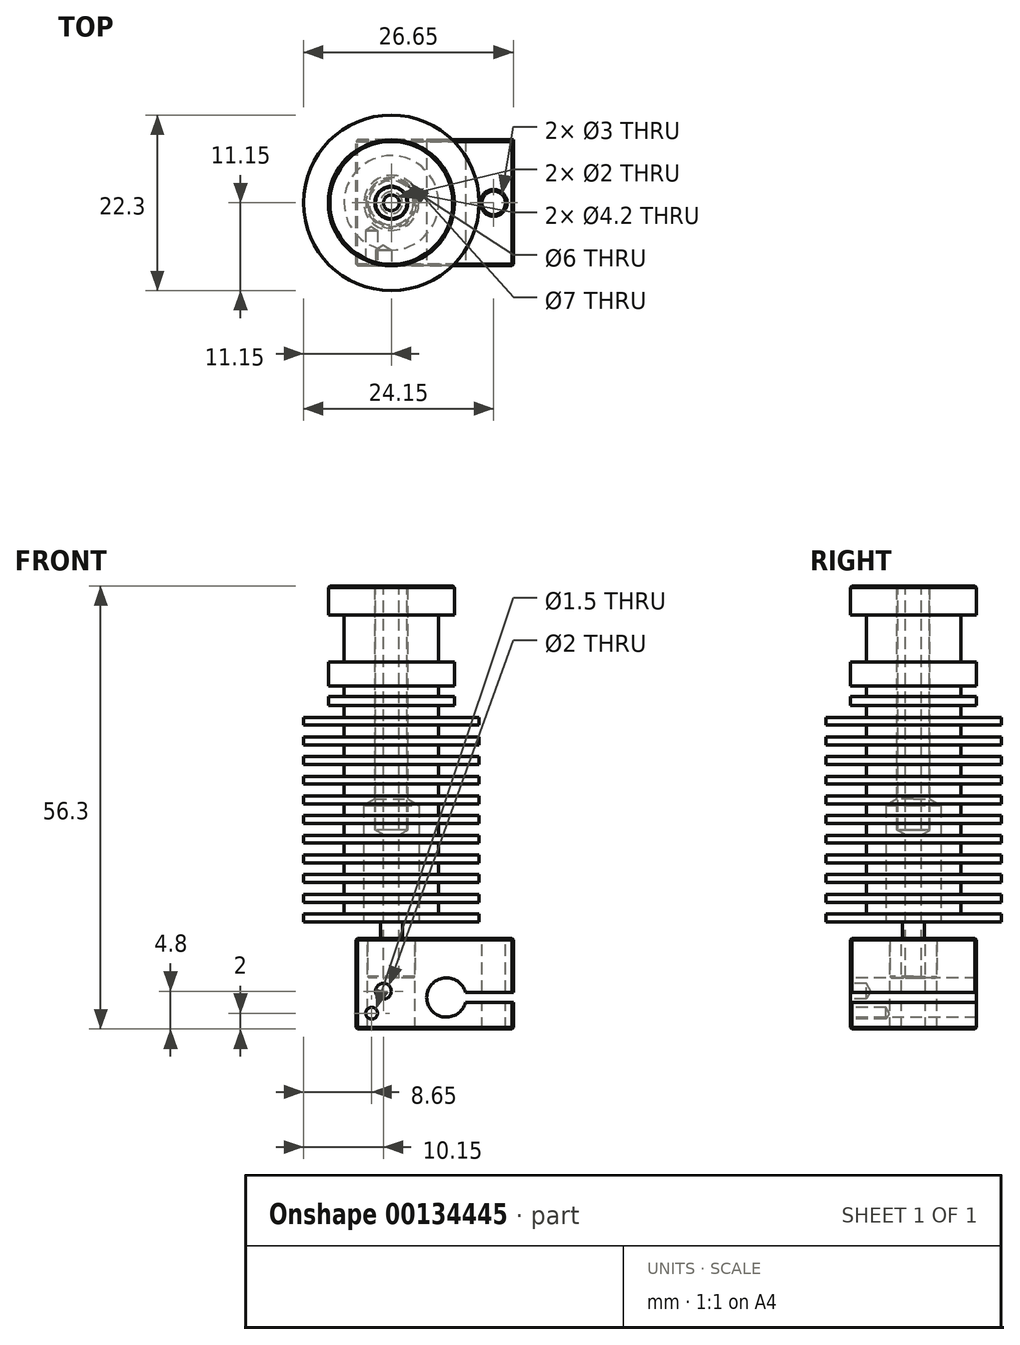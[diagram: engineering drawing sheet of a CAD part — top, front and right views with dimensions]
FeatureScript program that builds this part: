
annotation { "Feature Type Name" : "Feature", "Feature Type Description" : "" }
export const myFeature = defineFeature(function(context is Context, id is Id, definition is map)
    precondition{}
    {
        {
            var Q0;
            Q0=qCreatedBy(makeId("Front.planeOp"),FACE);
            var sketch = newSketch(context, id + "F0", { "sketchPlane" : qUnion([Q0])});
            skLineSegment(sketch, "E0", {"start": v(0, 21.35) * mm, "end": v(8, 21.35) * mm});
            skLineSegment(sketch, "E1", {"start": v(8, 21.35) * mm, "end": v(8, 17.65) * mm});
            skLineSegment(sketch, "E2", {"start": v(8, 17.65) * mm, "end": v(6, 17.65) * mm});
            skLineSegment(sketch, "E3", {"start": v(6, 17.65) * mm, "end": v(6, 11.65) * mm});
            skLineSegment(sketch, "E4", {"start": v(6, 11.65) * mm, "end": v(8, 11.65) * mm});
            skLineSegment(sketch, "E5", {"start": v(8, 11.65) * mm, "end": v(8, 8.65) * mm});
            skLineSegment(sketch, "E6", {"start": v(8, 8.65) * mm, "end": v(6, 8.65) * mm});
            skLineSegment(sketch, "E7", {"start": v(6, 8.65) * mm, "end": v(6, 7.3) * mm});
            skLineSegment(sketch, "E8", {"start": v(6, 7.3) * mm, "end": v(8, 7.3) * mm});
            skLineSegment(sketch, "E9", {"start": v(8, 7.3) * mm, "end": v(8, 6.15) * mm});
            skLineSegment(sketch, "E10", {"start": v(8, 6.15) * mm, "end": v(6, 6.15) * mm});
            skLineSegment(sketch, "E11", {"start": v(6, 6.15) * mm, "end": v(6, 4.65) * mm});
            skLineSegment(sketch, "E12", {"start": v(6, 4.65) * mm, "end": v(11.15, 4.65) * mm});
            skLineSegment(sketch, "E13", {"start": v(11.15, 4.65) * mm, "end": v(11.15, 3.65) * mm});
            skLineSegment(sketch, "E14", {"start": v(11.15, 3.65) * mm, "end": v(6, 3.65) * mm});
            skLineSegment(sketch, "E15.0.1.0", {"start": v(6, 3.65) * mm, "end": v(6, 2.15) * mm});
            skLineSegment(sketch, "E15.0.1.1", {"start": v(6, 2.15) * mm, "end": v(11.15, 2.15) * mm});
            skLineSegment(sketch, "E15.0.1.2", {"start": v(11.15, 2.15) * mm, "end": v(11.15, 1.15) * mm});
            skLineSegment(sketch, "E15.0.1.3", {"start": v(11.15, 1.15) * mm, "end": v(6, 1.15) * mm});
            skLineSegment(sketch, "E15.0.2.0", {"start": v(6, 1.15) * mm, "end": v(6, -0.35) * mm});
            skLineSegment(sketch, "E15.0.2.1", {"start": v(6, -0.35) * mm, "end": v(11.15, -0.35) * mm});
            skLineSegment(sketch, "E15.0.2.2", {"start": v(11.15, -0.35) * mm, "end": v(11.15, -1.35) * mm});
            skLineSegment(sketch, "E15.0.2.3", {"start": v(11.15, -1.35) * mm, "end": v(6, -1.35) * mm});
            skLineSegment(sketch, "E15.0.3.0", {"start": v(6, -1.35) * mm, "end": v(6, -2.85) * mm});
            skLineSegment(sketch, "E15.0.3.1", {"start": v(6, -2.85) * mm, "end": v(11.15, -2.85) * mm});
            skLineSegment(sketch, "E15.0.3.2", {"start": v(11.15, -2.85) * mm, "end": v(11.15, -3.85) * mm});
            skLineSegment(sketch, "E15.0.3.3", {"start": v(11.15, -3.85) * mm, "end": v(6, -3.85) * mm});
            skLineSegment(sketch, "E15.0.4.0", {"start": v(6, -3.85) * mm, "end": v(6, -5.35) * mm});
            skLineSegment(sketch, "E15.0.4.1", {"start": v(6, -5.35) * mm, "end": v(11.15, -5.35) * mm});
            skLineSegment(sketch, "E15.0.4.2", {"start": v(11.15, -5.35) * mm, "end": v(11.15, -6.35) * mm});
            skLineSegment(sketch, "E15.0.4.3", {"start": v(11.15, -6.35) * mm, "end": v(6, -6.35) * mm});
            skLineSegment(sketch, "E15.0.5.0", {"start": v(6, -6.35) * mm, "end": v(6, -7.85) * mm});
            skLineSegment(sketch, "E15.0.5.1", {"start": v(6, -7.85) * mm, "end": v(11.15, -7.85) * mm});
            skLineSegment(sketch, "E15.0.5.2", {"start": v(11.15, -7.85) * mm, "end": v(11.15, -8.85) * mm});
            skLineSegment(sketch, "E15.0.5.3", {"start": v(11.15, -8.85) * mm, "end": v(6, -8.85) * mm});
            skLineSegment(sketch, "E15.0.6.0", {"start": v(6, -8.85) * mm, "end": v(6, -10.35) * mm});
            skLineSegment(sketch, "E15.0.6.1", {"start": v(6, -10.35) * mm, "end": v(11.15, -10.35) * mm});
            skLineSegment(sketch, "E15.0.6.2", {"start": v(11.15, -10.35) * mm, "end": v(11.15, -11.35) * mm});
            skLineSegment(sketch, "E15.0.6.3", {"start": v(11.15, -11.35) * mm, "end": v(6, -11.35) * mm});
            skLineSegment(sketch, "E15.0.7.0", {"start": v(6, -11.35) * mm, "end": v(6, -12.85) * mm});
            skLineSegment(sketch, "E15.0.7.1", {"start": v(6, -12.85) * mm, "end": v(11.15, -12.85) * mm});
            skLineSegment(sketch, "E15.0.7.2", {"start": v(11.15, -12.85) * mm, "end": v(11.15, -13.85) * mm});
            skLineSegment(sketch, "E15.0.7.3", {"start": v(11.15, -13.85) * mm, "end": v(6, -13.85) * mm});
            skLineSegment(sketch, "E15.0.8.0", {"start": v(6, -13.85) * mm, "end": v(6, -15.35) * mm});
            skLineSegment(sketch, "E15.0.8.1", {"start": v(6, -15.35) * mm, "end": v(11.15, -15.35) * mm});
            skLineSegment(sketch, "E15.0.8.2", {"start": v(11.15, -15.35) * mm, "end": v(11.15, -16.35) * mm});
            skLineSegment(sketch, "E15.0.8.3", {"start": v(11.15, -16.35) * mm, "end": v(6, -16.35) * mm});
            skLineSegment(sketch, "E15.0.9.0", {"start": v(6, -16.35) * mm, "end": v(6, -17.85) * mm});
            skLineSegment(sketch, "E15.0.9.1", {"start": v(6, -17.85) * mm, "end": v(11.15, -17.85) * mm});
            skLineSegment(sketch, "E15.0.9.2", {"start": v(11.15, -17.85) * mm, "end": v(11.15, -18.85) * mm});
            skLineSegment(sketch, "E15.0.9.3", {"start": v(11.15, -18.85) * mm, "end": v(6, -18.85) * mm});
            skLineSegment(sketch, "E15.direction1", {"start": v(6, 3.65) * mm, "end": v(31, 3.65) * mm, "construction": true});
            skLineSegment(sketch, "E15.direction2", {"start": v(6, 3.65) * mm, "end": v(6, 1.15) * mm, "construction": true});
            skLineSegment(sketch, "E16", {"start": v(6, -18.85) * mm, "end": v(6, -20.35) * mm});
            skLineSegment(sketch, "E17", {"start": v(6, -20.35) * mm, "end": v(11.15, -20.35) * mm});
            skLineSegment(sketch, "E18", {"start": v(11.15, -20.35) * mm, "end": v(11.15, -21.35) * mm});
            skLineSegment(sketch, "E19", {"start": v(11.15, -21.35) * mm, "end": v(0, -21.35) * mm});
            skLineSegment(sketch, "E20", {"start": v(0, 21.35) * mm, "end": v(0, -21.35) * mm});
            skPoint(sketch, "E21.orphan", {"position": v(6, -21.35) * mm});
            skSolve(sketch);
        }
        {
            var Q0;
            Q0=makeQuery(id+"F0.imprint","IMPRINT",FACE,{"disambiguationData":[TD([[makeQuery(id+"F0.imprint","IMPRINT",EDGE,{"derivedFrom":sQuery(id+"F0.wireOp",EDGE,"E0")}),-1.0]])]});
            var Q1;
            Q1=sQuery(id+"F0.wireOp",EDGE,"E20");
            revolve(context, id + "F1", {"entities" : qUnion([Q0]), "axis" : qUnion([Q1]), "revolveType" : RevolveType.FULL});
        }
        {
            var Q0;
            Q0=makeQuery(id+"F1.opRevolve","SWEPT_FACE",FACE,{"disambiguationData":[OSD([sQuery(id+"F0.wireOp",EDGE,"E19")])]});
            var sketch = newSketch(context, id + "F2", { "sketchPlane" : qUnion([Q0])});
            skPoint(sketch, "E22", {"position": v(0, 0) * mm});
            skSolve(sketch);
        }
        {
            var Q0;
            Q0=sQuery(id+"F2.wireOp",VERTEX,"E22");
            var Q1;
            Q1=makeQuery(id+"F1.opRevolve","SWEPT_BODY",BODY,{"disambiguationData":[OSD([sQuery(id+"F0.wireOp",EDGE,"E0"),sQuery(id+"F0.wireOp",EDGE,"E1"),sQuery(id+"F0.wireOp",EDGE,"E2"),sQuery(id+"F0.wireOp",EDGE,"E3"),sQuery(id+"F0.wireOp",EDGE,"E4"),sQuery(id+"F0.wireOp",EDGE,"E5"),sQuery(id+"F0.wireOp",EDGE,"E6"),sQuery(id+"F0.wireOp",EDGE,"E7"),sQuery(id+"F0.wireOp",EDGE,"E8"),sQuery(id+"F0.wireOp",EDGE,"E9"),sQuery(id+"F0.wireOp",EDGE,"E10"),sQuery(id+"F0.wireOp",EDGE,"E11"),sQuery(id+"F0.wireOp",EDGE,"E12"),sQuery(id+"F0.wireOp",EDGE,"E13"),sQuery(id+"F0.wireOp",EDGE,"E14"),sQuery(id+"F0.wireOp",EDGE,"E15.0.1.0"),sQuery(id+"F0.wireOp",EDGE,"E15.0.1.1"),sQuery(id+"F0.wireOp",EDGE,"E15.0.1.2"),sQuery(id+"F0.wireOp",EDGE,"E15.0.1.3"),sQuery(id+"F0.wireOp",EDGE,"E15.0.2.0"),sQuery(id+"F0.wireOp",EDGE,"E15.0.2.1"),sQuery(id+"F0.wireOp",EDGE,"E15.0.2.2"),sQuery(id+"F0.wireOp",EDGE,"E15.0.2.3"),sQuery(id+"F0.wireOp",EDGE,"E15.0.3.0"),sQuery(id+"F0.wireOp",EDGE,"E15.0.3.1"),sQuery(id+"F0.wireOp",EDGE,"E15.0.3.2"),sQuery(id+"F0.wireOp",EDGE,"E15.0.3.3"),sQuery(id+"F0.wireOp",EDGE,"E15.0.4.0"),sQuery(id+"F0.wireOp",EDGE,"E15.0.4.1"),sQuery(id+"F0.wireOp",EDGE,"E15.0.4.2"),sQuery(id+"F0.wireOp",EDGE,"E15.0.4.3"),sQuery(id+"F0.wireOp",EDGE,"E15.0.5.0"),sQuery(id+"F0.wireOp",EDGE,"E15.0.5.1"),sQuery(id+"F0.wireOp",EDGE,"E15.0.5.2"),sQuery(id+"F0.wireOp",EDGE,"E15.0.5.3"),sQuery(id+"F0.wireOp",EDGE,"E15.0.6.0"),sQuery(id+"F0.wireOp",EDGE,"E15.0.6.1"),sQuery(id+"F0.wireOp",EDGE,"E15.0.6.2"),sQuery(id+"F0.wireOp",EDGE,"E15.0.6.3"),sQuery(id+"F0.wireOp",EDGE,"E15.0.7.0"),sQuery(id+"F0.wireOp",EDGE,"E15.0.7.1"),sQuery(id+"F0.wireOp",EDGE,"E15.0.7.2"),sQuery(id+"F0.wireOp",EDGE,"E15.0.7.3"),sQuery(id+"F0.wireOp",EDGE,"E15.0.8.0"),sQuery(id+"F0.wireOp",EDGE,"E15.0.8.1"),sQuery(id+"F0.wireOp",EDGE,"E15.0.8.2"),sQuery(id+"F0.wireOp",EDGE,"E15.0.8.3"),sQuery(id+"F0.wireOp",EDGE,"E15.0.9.0"),sQuery(id+"F0.wireOp",EDGE,"E15.0.9.1"),sQuery(id+"F0.wireOp",EDGE,"E15.0.9.2"),sQuery(id+"F0.wireOp",EDGE,"E15.0.9.3"),sQuery(id+"F0.wireOp",EDGE,"E16"),sQuery(id+"F0.wireOp",EDGE,"E17"),sQuery(id+"F0.wireOp",EDGE,"E18"),sQuery(id+"F0.wireOp",EDGE,"E19"),sQuery(id+"F0.wireOp",EDGE,"E20")])]});
            hole(context, id + "F3", {"style" : HoleStyle.SIMPLE, "endStyle" : HoleEndStyle.BLIND, "holeDiameter" : 7 * mm, "holeDepth" : 14.8 * mm, "locations" : qUnion([Q0]), "scope" : qUnion([Q1])});
        }
        {
            var Q0;
            Q0=qCreatedBy(makeId("Front.planeOp"),FACE);
            var sketch = newSketch(context, id + "F4", { "sketchPlane" : qUnion([Q0])});
            skLineSegment(sketch, "E23", {"start": v(0, -6.55) * mm, "end": v(3.5, -6.55) * mm});
            skLineSegment(sketch, "E24", {"start": v(3.5, -6.55) * mm, "end": v(3.5, -21.35) * mm});
            skLineSegment(sketch, "E25", {"start": v(3.5, -21.35) * mm, "end": v(1.4, -21.35) * mm});
            skLineSegment(sketch, "E26", {"start": v(1.4, -21.35) * mm, "end": v(1.4, -23.45) * mm});
            skLineSegment(sketch, "E27", {"start": v(1.4, -23.45) * mm, "end": v(3, -23.45) * mm});
            skLineSegment(sketch, "E28", {"start": v(3, -23.45) * mm, "end": v(3, -28.45) * mm});
            skLineSegment(sketch, "E29", {"start": v(3, -28.45) * mm, "end": v(0, -28.45) * mm});
            skLineSegment(sketch, "E30", {"start": v(0, -28.45) * mm, "end": v(0, -6.55) * mm});
            skLineSegment(sketch, "E31.0", {"start": v(3.5, -21.35) * mm, "end": v(-3.5, -21.35) * mm, "construction": true});
            skSolve(sketch);
        }
        {
            var Q0;
            Q0=qSketchRegion(id+"F4",true);
            var Q1;
            Q1=sQuery(id+"F4.wireOp",EDGE,"E30");
            revolve(context, id + "F5", {"entities" : qUnion([Q0]), "axis" : qUnion([Q1]), "revolveType" : RevolveType.FULL});
        }
        {
            var Q0;
            Q0=makeQuery(id+"F5.opRevolve","SWEPT_FACE",FACE,{"disambiguationData":[OSD([sQuery(id+"F4.wireOp",EDGE,"E23")])]});
            var sketch = newSketch(context, id + "F6", { "sketchPlane" : qUnion([Q0])});
            skPoint(sketch, "E32", {"position": v(0, 0) * mm});
            skSolve(sketch);
        }
        {
            var Q0;
            Q0=sQuery(id+"F6.wireOp",VERTEX,"E32");
            var Q1;
            Q1=makeQuery(id+"F5.opRevolve","SWEPT_BODY",BODY,{"disambiguationData":[OSD([sQuery(id+"F4.wireOp",EDGE,"E23"),sQuery(id+"F4.wireOp",EDGE,"E24"),sQuery(id+"F4.wireOp",EDGE,"E25"),sQuery(id+"F4.wireOp",EDGE,"E26"),sQuery(id+"F4.wireOp",EDGE,"E27"),sQuery(id+"F4.wireOp",EDGE,"E28"),sQuery(id+"F4.wireOp",EDGE,"E29"),sQuery(id+"F4.wireOp",EDGE,"E30")])]});
            hole(context, id + "F7", {"style" : HoleStyle.SIMPLE, "endStyle" : HoleEndStyle.THROUGH, "holeDiameter" : 2 * mm, "locations" : qUnion([Q0]), "scope" : qUnion([Q1]), "isTappedThrough" : true});
        }
        {
            var Q0;
            Q0=makeQuery(id+"F1.opRevolve","SWEPT_FACE",FACE,{"disambiguationData":[OSD([sQuery(id+"F0.wireOp",EDGE,"E0")])]});
            var sketch = newSketch(context, id + "F8", { "sketchPlane" : qUnion([Q0])});
            skPoint(sketch, "E33", {"position": v(0, 0) * mm});
            skSolve(sketch);
        }
        {
            var Q0;
            Q0=sQuery(id+"F8.wireOp",VERTEX,"E33");
            var Q1;
            Q1=makeQuery(id+"F1.opRevolve","SWEPT_BODY",BODY,{"disambiguationData":[OSD([sQuery(id+"F0.wireOp",EDGE,"E0"),sQuery(id+"F0.wireOp",EDGE,"E1"),sQuery(id+"F0.wireOp",EDGE,"E2"),sQuery(id+"F0.wireOp",EDGE,"E3"),sQuery(id+"F0.wireOp",EDGE,"E4"),sQuery(id+"F0.wireOp",EDGE,"E5"),sQuery(id+"F0.wireOp",EDGE,"E6"),sQuery(id+"F0.wireOp",EDGE,"E7"),sQuery(id+"F0.wireOp",EDGE,"E8"),sQuery(id+"F0.wireOp",EDGE,"E9"),sQuery(id+"F0.wireOp",EDGE,"E10"),sQuery(id+"F0.wireOp",EDGE,"E11"),sQuery(id+"F0.wireOp",EDGE,"E12"),sQuery(id+"F0.wireOp",EDGE,"E13"),sQuery(id+"F0.wireOp",EDGE,"E14"),sQuery(id+"F0.wireOp",EDGE,"E15.0.1.0"),sQuery(id+"F0.wireOp",EDGE,"E15.0.1.1"),sQuery(id+"F0.wireOp",EDGE,"E15.0.1.2"),sQuery(id+"F0.wireOp",EDGE,"E15.0.1.3"),sQuery(id+"F0.wireOp",EDGE,"E15.0.2.0"),sQuery(id+"F0.wireOp",EDGE,"E15.0.2.1"),sQuery(id+"F0.wireOp",EDGE,"E15.0.2.2"),sQuery(id+"F0.wireOp",EDGE,"E15.0.2.3"),sQuery(id+"F0.wireOp",EDGE,"E15.0.3.0"),sQuery(id+"F0.wireOp",EDGE,"E15.0.3.1"),sQuery(id+"F0.wireOp",EDGE,"E15.0.3.2"),sQuery(id+"F0.wireOp",EDGE,"E15.0.3.3"),sQuery(id+"F0.wireOp",EDGE,"E15.0.4.0"),sQuery(id+"F0.wireOp",EDGE,"E15.0.4.1"),sQuery(id+"F0.wireOp",EDGE,"E15.0.4.2"),sQuery(id+"F0.wireOp",EDGE,"E15.0.4.3"),sQuery(id+"F0.wireOp",EDGE,"E15.0.5.0"),sQuery(id+"F0.wireOp",EDGE,"E15.0.5.1"),sQuery(id+"F0.wireOp",EDGE,"E15.0.5.2"),sQuery(id+"F0.wireOp",EDGE,"E15.0.5.3"),sQuery(id+"F0.wireOp",EDGE,"E15.0.6.0"),sQuery(id+"F0.wireOp",EDGE,"E15.0.6.1"),sQuery(id+"F0.wireOp",EDGE,"E15.0.6.2"),sQuery(id+"F0.wireOp",EDGE,"E15.0.6.3"),sQuery(id+"F0.wireOp",EDGE,"E15.0.7.0"),sQuery(id+"F0.wireOp",EDGE,"E15.0.7.1"),sQuery(id+"F0.wireOp",EDGE,"E15.0.7.2"),sQuery(id+"F0.wireOp",EDGE,"E15.0.7.3"),sQuery(id+"F0.wireOp",EDGE,"E15.0.8.0"),sQuery(id+"F0.wireOp",EDGE,"E15.0.8.1"),sQuery(id+"F0.wireOp",EDGE,"E15.0.8.2"),sQuery(id+"F0.wireOp",EDGE,"E15.0.8.3"),sQuery(id+"F0.wireOp",EDGE,"E15.0.9.0"),sQuery(id+"F0.wireOp",EDGE,"E15.0.9.1"),sQuery(id+"F0.wireOp",EDGE,"E15.0.9.2"),sQuery(id+"F0.wireOp",EDGE,"E15.0.9.3"),sQuery(id+"F0.wireOp",EDGE,"E16"),sQuery(id+"F0.wireOp",EDGE,"E17"),sQuery(id+"F0.wireOp",EDGE,"E18"),sQuery(id+"F0.wireOp",EDGE,"E19"),sQuery(id+"F0.wireOp",EDGE,"E20")])]});
            var Q2;
            Q2=makeQuery(id+"F5.opRevolve","SWEPT_BODY",BODY,{"disambiguationData":[OSD([sQuery(id+"F4.wireOp",EDGE,"E23"),sQuery(id+"F4.wireOp",EDGE,"E24"),sQuery(id+"F4.wireOp",EDGE,"E25"),sQuery(id+"F4.wireOp",EDGE,"E26"),sQuery(id+"F4.wireOp",EDGE,"E27"),sQuery(id+"F4.wireOp",EDGE,"E28"),sQuery(id+"F4.wireOp",EDGE,"E29"),sQuery(id+"F4.wireOp",EDGE,"E30")])]});
            hole(context, id + "F9", {"style" : HoleStyle.SIMPLE, "endStyle" : HoleEndStyle.BLIND, "holeDiameter" : 4.2 * mm, "holeDepth" : 31 * mm, "locations" : qUnion([Q0]), "scope" : qUnion([Q1, Q2])});
        }
        {
            var Q0;
            Q0=qCreatedBy(makeId("Front.planeOp"),FACE);
            var sketch = newSketch(context, id + "F10", { "sketchPlane" : qUnion([Q0])});
            skLineSegment(sketch, "E34.0", {"start": v(-2.1, -9.65) * mm, "end": v(2.1, -9.65) * mm, "construction": true});
            skLineSegment(sketch, "E35.bottom", {"start": v(1, 21.35) * mm, "end": v(2, 21.35) * mm});
            skLineSegment(sketch, "E35.top", {"start": v(1, -9.65) * mm, "end": v(2, -9.65) * mm});
            skLineSegment(sketch, "E35.left", {"start": v(1, 21.35) * mm, "end": v(1, -9.65) * mm});
            skLineSegment(sketch, "E35.right", {"start": v(2, 21.35) * mm, "end": v(2, -9.65) * mm});
            skLineSegment(sketch, "E36", {"start": v(0, 26.07) * mm, "end": v(0, -35.6) * mm, "construction": true});
            skLineSegment(sketch, "E37.0", {"start": v(-2.1, 21.35) * mm, "end": v(2.1, 21.35) * mm, "construction": true});
            skSolve(sketch);
        }
        {
            var Q0;
            Q0=qSketchRegion(id+"F10",true);
            var Q1;
            Q1=qConstructionFilter(qBodyType(qCreatedBy(id+"F10",EDGE),BodyType.WIRE),ConstructionObject.NO);
            var Q2;
            Q2=sQuery(id+"F10.wireOp",EDGE,"E36");
            revolve(context, id + "F11", {"entities" : qUnion([Q0]), "surfaceEntities" : qUnion([Q1]), "axis" : qUnion([Q2]), "revolveType" : RevolveType.FULL});
        }
        {
            var Q0;
            Q0=makeQuery(id+"F5.opRevolve","SWEPT_FACE",FACE,{"disambiguationData":[OSD([sQuery(id+"F4.wireOp",EDGE,"E27")])]});
            var sketch = newSketch(context, id + "F12", { "sketchPlane" : qUnion([Q0])});
            skLineSegment(sketch, "E38.bottom", {"start": v(-4.5, -8) * mm, "end": v(15.5, -8) * mm});
            skLineSegment(sketch, "E38.top", {"start": v(-4.5, 8) * mm, "end": v(15.5, 8) * mm});
            skLineSegment(sketch, "E38.left", {"start": v(-4.5, -8) * mm, "end": v(-4.5, 8) * mm});
            skLineSegment(sketch, "E38.right", {"start": v(15.5, -8) * mm, "end": v(15.5, 8) * mm});
            skPoint(sketch, "E39", {"position": v(0, 0) * mm});
            skPoint(sketch, "E40", {"position": v(13, 0) * mm});
            skSolve(sketch);
        }
        {
            var Q0;
            Q0=qSketchRegion(id+"F12",true);
            extrude(context, id + "F13", {"entities" : qUnion([Q0]), "oppositeDirection" : true, "depth" : 11.5 * mm});
        }
        {
            var Q0;
            Q0=sQuery(id+"F12.wireOp",VERTEX,"E39");
            var Q1;
            Q1=makeQuery(id+"F13.opExtrude","SWEPT_BODY",BODY,{"disambiguationData":[OSD([sQuery(id+"F12.wireOp",EDGE,"E38.bottom"),sQuery(id+"F12.wireOp",EDGE,"E38.top"),sQuery(id+"F12.wireOp",EDGE,"E38.left"),sQuery(id+"F12.wireOp",EDGE,"E38.right")])]});
            hole(context, id + "F14", {"style" : HoleStyle.SIMPLE, "endStyle" : HoleEndStyle.THROUGH, "holeDiameter" : 6 * mm, "locations" : qUnion([Q0]), "scope" : qUnion([Q1]), "isTappedThrough" : true});
        }
        {
            var Q0;
            Q0=sQuery(id+"F12.wireOp",VERTEX,"E40");
            var Q1;
            Q1=makeQuery(id+"F13.opExtrude","SWEPT_BODY",BODY,{"disambiguationData":[OSD([sQuery(id+"F12.wireOp",EDGE,"E38.bottom"),sQuery(id+"F12.wireOp",EDGE,"E38.top"),sQuery(id+"F12.wireOp",EDGE,"E38.left"),sQuery(id+"F12.wireOp",EDGE,"E38.right")])]});
            hole(context, id + "F15", {"style" : HoleStyle.SIMPLE, "endStyle" : HoleEndStyle.THROUGH, "holeDiameter" : 3 * mm, "locations" : qUnion([Q0]), "scope" : qUnion([Q1]), "isTappedThrough" : true});
        }
        {
            var Q0;
            Q0=makeQuery(id+"F13.opExtrude","SWEPT_FACE",FACE,{"disambiguationData":[OSD([sQuery(id+"F12.wireOp",EDGE,"E38.bottom")])]});
            var sketch = newSketch(context, id + "F16", { "sketchPlane" : qUnion([Q0])});
            skPoint(sketch, "E41", {"position": v(-1, -30.15) * mm});
            skPoint(sketch, "E42", {"position": v(-2.5, -32.95) * mm});
            skPoint(sketch, "E43", {"position": v(7, -30.95) * mm});
            skLineSegment(sketch, "E44.bottom", {"start": v(15.5, -30.3) * mm, "end": v(7, -30.3) * mm});
            skLineSegment(sketch, "E44.top", {"start": v(15.5, -31.6) * mm, "end": v(7, -31.6) * mm});
            skLineSegment(sketch, "E44.left", {"start": v(15.5, -30.3) * mm, "end": v(15.5, -31.6) * mm});
            skLineSegment(sketch, "E44.right", {"start": v(7, -30.3) * mm, "end": v(7, -31.6) * mm});
            skSolve(sketch);
        }
        {
            var Q0;
            Q0=sQuery(id+"F16.wireOp",VERTEX,"E42");
            var Q1;
            Q1=makeQuery(id+"F13.opExtrude","SWEPT_BODY",BODY,{"disambiguationData":[OSD([sQuery(id+"F12.wireOp",EDGE,"E38.bottom"),sQuery(id+"F12.wireOp",EDGE,"E38.top"),sQuery(id+"F12.wireOp",EDGE,"E38.left"),sQuery(id+"F12.wireOp",EDGE,"E38.right")])]});
            hole(context, id + "F17", {"style" : HoleStyle.SIMPLE, "endStyle" : HoleEndStyle.BLIND, "holeDiameter" : 1.5 * mm, "holeDepth" : 4.5 * mm, "locations" : qUnion([Q0]), "scope" : qUnion([Q1])});
        }
        {
            var Q0;
            Q0=sQuery(id+"F16.wireOp",VERTEX,"E41");
            var Q1;
            Q1=makeQuery(id+"F13.opExtrude","SWEPT_BODY",BODY,{"disambiguationData":[OSD([sQuery(id+"F12.wireOp",EDGE,"E38.bottom"),sQuery(id+"F12.wireOp",EDGE,"E38.top"),sQuery(id+"F12.wireOp",EDGE,"E38.left"),sQuery(id+"F12.wireOp",EDGE,"E38.right")])]});
            hole(context, id + "F18", {"style" : HoleStyle.SIMPLE, "endStyle" : HoleEndStyle.BLIND, "holeDiameter" : 2 * mm, "holeDepth" : 2 * mm, "locations" : qUnion([Q0]), "scope" : qUnion([Q1])});
        }
        {
            var Q0;
            Q0=sQuery(id+"F16.wireOp",VERTEX,"E43");
            var Q1;
            Q1=makeQuery(id+"F13.opExtrude","SWEPT_BODY",BODY,{"disambiguationData":[OSD([sQuery(id+"F12.wireOp",EDGE,"E38.bottom"),sQuery(id+"F12.wireOp",EDGE,"E38.top"),sQuery(id+"F12.wireOp",EDGE,"E38.left"),sQuery(id+"F12.wireOp",EDGE,"E38.right")])]});
            hole(context, id + "F19", {"style" : HoleStyle.SIMPLE, "endStyle" : HoleEndStyle.THROUGH, "holeDiameter" : 5 * mm, "locations" : qUnion([Q0]), "scope" : qUnion([Q1]), "isTappedThrough" : true});
        }
        {
            var Q0;
            Q0=makeQuery(id+"F16.imprint","IMPRINT",FACE,{"disambiguationData":[TD([[makeQuery(id+"F16.imprint","IMPRINT",EDGE,{"derivedFrom":sQuery(id+"F16.wireOp",EDGE,"E44.bottom")}),1.0]])]});
            var Q1;
            Q1=makeQuery(id+"F13.opExtrude","SWEPT_BODY",BODY,{"disambiguationData":[OSD([sQuery(id+"F12.wireOp",EDGE,"E38.bottom"),sQuery(id+"F12.wireOp",EDGE,"E38.top"),sQuery(id+"F12.wireOp",EDGE,"E38.left"),sQuery(id+"F12.wireOp",EDGE,"E38.right")])]});
            extrude(context, id + "F20", {"entities" : qUnion([Q0]), "operationType" : NewBodyOperationType.REMOVE, "endBound" : BoundingType.UP_TO_BODY, "oppositeDirection" : true, "endBoundEntityBody" : qUnion([Q1]), "depth" : 25 * mm});
        }
        {
            var Q0;
            Q0=makeQuery(id+"F1.opRevolve","SWEPT_EDGE",EDGE,{"disambiguationData":[OSD([sQuery(id+"F0.wireOp",EDGE,"E0"),sQuery(id+"F0.wireOp",EDGE,"E1")])]});
            var Q1;
            Q1=makeQuery(id+"F3.hole-0.boolean.opBoolean","COPY",EDGE,{"derivedFrom":makeQuery(id+"F3.hole-0.opRevolve","SWEPT_EDGE",EDGE,{"disambiguationData":[OSD([sQuery(id+"F3.hole-0.sketch.wireOp",EDGE,"core_line_2"),sQuery(id+"F3.hole-0.sketch.wireOp",EDGE,"core_line_3")])]})});
            var Q2;
            Q2=makeQuery(id+"F3.hole-0.boolean.opBoolean","COPY",EDGE,{"derivedFrom":makeQuery(id+"F3.hole-0.opRevolve","SWEPT_EDGE",EDGE,{"disambiguationData":[OSD([sQuery(id+"F3.hole-0.sketch.wireOp",EDGE,"core_line_1"),sQuery(id+"F3.hole-0.sketch.wireOp",EDGE,"core_line_2")])]})});
            var Q3;
            Q3=makeQuery(id+"F5.opRevolve","SWEPT_EDGE",EDGE,{"disambiguationData":[OSD([sQuery(id+"F4.wireOp",EDGE,"E27"),sQuery(id+"F4.wireOp",EDGE,"E28")])]});
            var Q4;
            Q4=makeQuery(id+"F5.opRevolve","SWEPT_EDGE",EDGE,{"disambiguationData":[OSD([sQuery(id+"F4.wireOp",EDGE,"E28"),sQuery(id+"F4.wireOp",EDGE,"E29")])]});
            var Q5;
            Q5=makeQuery(id+"F7.hole-0.boolean.opBoolean","INTERSECT",EDGE,{"derivedFrom":[makeQuery(id+"F5.opRevolve","SWEPT_FACE",FACE,{"disambiguationData":[OSD([sQuery(id+"F4.wireOp",EDGE,"E29")])]}),makeQuery(id+"F7.hole-0.opRevolve","SWEPT_FACE",FACE,{"disambiguationData":[OSD([sQuery(id+"F7.hole-0.sketch.wireOp",EDGE,"core_line_2")])]})]});
            var Q6;
            Q6=makeQuery(id+"F13.opExtrude","CAP_EDGE",EDGE,{"disambiguationData":[OSD([sQuery(id+"F12.wireOp",EDGE,"E38.left")])],"isStart":true});
            var Q7;
            Q7=makeQuery(id+"F13.opExtrude","CAP_EDGE",EDGE,{"disambiguationData":[OSD([sQuery(id+"F12.wireOp",EDGE,"E38.bottom")])],"isStart":true});
            var Q8;
            Q8=makeQuery(id+"F13.opExtrude","SWEPT_EDGE",EDGE,{"disambiguationData":[OSD([sQuery(id+"F12.wireOp",EDGE,"E38.bottom"),sQuery(id+"F12.wireOp",EDGE,"E38.left")])]});
            var Q9;
            {var subQ0=sQuery(id+"F12.wireOp",EDGE,"E38.bottom");var subQ1=sQuery(id+"F12.wireOp",EDGE,"E38.right");Q9=makeQuery(id+"F20.boolean.opBoolean","SPLIT",EDGE,{"disambiguationData":[TD([makeQuery(id+"F20.opExtrude","SWEPT_FACE",FACE,{"disambiguationData":[OSD([sQuery(id+"F16.wireOp",EDGE,"E44.bottom")])]})])],"derivedFrom":makeQuery(id+"F13.opExtrude","SWEPT_EDGE",EDGE,{"disambiguationData":[OSD([subQ0,subQ1])]})});}
            var Q10;
            {var subQ0=sQuery(id+"F12.wireOp",EDGE,"E38.right");var subQ1=sQuery(id+"F12.wireOp",EDGE,"E38.top");Q10=makeQuery(id+"F20.boolean.opBoolean","SPLIT",EDGE,{"disambiguationData":[TD([makeQuery(id+"F20.opExtrude","SWEPT_FACE",FACE,{"disambiguationData":[OSD([sQuery(id+"F16.wireOp",EDGE,"E44.bottom")])]})])],"derivedFrom":makeQuery(id+"F13.opExtrude","SWEPT_EDGE",EDGE,{"disambiguationData":[OSD([subQ1,subQ0])]})});}
            var Q11;
            Q11=makeQuery(id+"F13.opExtrude","CAP_EDGE",EDGE,{"disambiguationData":[OSD([sQuery(id+"F12.wireOp",EDGE,"E38.top")])],"isStart":true});
            var Q12;
            Q12=makeQuery(id+"F13.opExtrude","CAP_EDGE",EDGE,{"disambiguationData":[OSD([sQuery(id+"F12.wireOp",EDGE,"E38.right")])],"isStart":true});
            var Q13;
            Q13=makeQuery(id+"F13.opExtrude","CAP_EDGE",EDGE,{"disambiguationData":[OSD([sQuery(id+"F12.wireOp",EDGE,"E38.right")])],"isStart":false});
            var Q14;
            {var subQ0=sQuery(id+"F12.wireOp",EDGE,"E38.bottom");var subQ1=sQuery(id+"F12.wireOp",EDGE,"E38.right");Q14=makeQuery(id+"F20.boolean.opBoolean","SPLIT",EDGE,{"disambiguationData":[TD([makeQuery(id+"F20.opExtrude","SWEPT_FACE",FACE,{"disambiguationData":[OSD([sQuery(id+"F16.wireOp",EDGE,"E44.top")])]})])],"derivedFrom":makeQuery(id+"F13.opExtrude","SWEPT_EDGE",EDGE,{"disambiguationData":[OSD([subQ0,subQ1])]})});}
            var Q15;
            Q15=makeQuery(id+"F13.opExtrude","CAP_EDGE",EDGE,{"disambiguationData":[OSD([sQuery(id+"F12.wireOp",EDGE,"E38.bottom")])],"isStart":false});
            var Q16;
            Q16=makeQuery(id+"F13.opExtrude","SWEPT_EDGE",EDGE,{"disambiguationData":[OSD([sQuery(id+"F12.wireOp",EDGE,"E38.top"),sQuery(id+"F12.wireOp",EDGE,"E38.left")])]});
            var Q17;
            Q17=makeQuery(id+"F13.opExtrude","CAP_EDGE",EDGE,{"disambiguationData":[OSD([sQuery(id+"F12.wireOp",EDGE,"E38.top")])],"isStart":false});
            var Q18;
            Q18=makeQuery(id+"F13.opExtrude","CAP_EDGE",EDGE,{"disambiguationData":[OSD([sQuery(id+"F12.wireOp",EDGE,"E38.left")])],"isStart":false});
            var Q19;
            Q19=makeQuery(id+"F17.hole-0.boolean.opBoolean","COPY",EDGE,{"derivedFrom":makeQuery(id+"F17.hole-0.opRevolve","SWEPT_EDGE",EDGE,{"disambiguationData":[OSD([sQuery(id+"F17.hole-0.sketch.wireOp",EDGE,"core_line_2"),sQuery(id+"F17.hole-0.sketch.wireOp",EDGE,"core_line_3")])]})});
            var Q20;
            Q20=makeQuery(id+"F18.hole-0.boolean.opBoolean","COPY",FACE,{"derivedFrom":makeQuery(id+"F18.hole-0.opRevolve","SWEPT_FACE",FACE,{"disambiguationData":[OSD([sQuery(id+"F18.hole-0.sketch.wireOp",EDGE,"core_line_2")])]})});
            var Q21;
            Q21=makeQuery(id+"F19.hole-0.boolean.opBoolean","COPY",EDGE,{"derivedFrom":makeQuery(id+"F19.hole-0.opRevolve","SWEPT_EDGE",EDGE,{"disambiguationData":[OSD([sQuery(id+"F19.hole-0.sketch.wireOp",EDGE,"core_line_2"),sQuery(id+"F19.hole-0.sketch.wireOp",EDGE,"core_line_3")])]})});
            var Q22;
            Q22=makeQuery(id+"F15.hole-0.boolean.opBoolean","COPY",EDGE,{"derivedFrom":makeQuery(id+"F15.hole-0.opRevolve","SWEPT_EDGE",EDGE,{"disambiguationData":[OSD([sQuery(id+"F15.hole-0.sketch.wireOp",EDGE,"core_line_2"),sQuery(id+"F15.hole-0.sketch.wireOp",EDGE,"core_line_3")])]})});
            var Q23;
            Q23=makeQuery(id+"F13.opExtrude","CAP_FACE",FACE,{"disambiguationData":[OSD([sQuery(id+"F12.wireOp",EDGE,"E38.bottom"),sQuery(id+"F12.wireOp",EDGE,"E38.top"),sQuery(id+"F12.wireOp",EDGE,"E38.left"),sQuery(id+"F12.wireOp",EDGE,"E38.right")])],"isStart":true});
            var Q24;
            Q24=makeQuery(id+"F19.hole-0.boolean.opBoolean","INTERSECT",EDGE,{"derivedFrom":[makeQuery(id+"F13.opExtrude","SWEPT_FACE",FACE,{"disambiguationData":[OSD([sQuery(id+"F12.wireOp",EDGE,"E38.top")])]}),makeQuery(id+"F19.hole-0.opRevolve","SWEPT_FACE",FACE,{"disambiguationData":[OSD([sQuery(id+"F19.hole-0.sketch.wireOp",EDGE,"core_line_2")])]})]});
            var Q25;
            Q25=makeQuery(id+"F15.hole-0.boolean.opBoolean","INTERSECT",EDGE,{"derivedFrom":[makeQuery(id+"F13.opExtrude","CAP_FACE",FACE,{"disambiguationData":[OSD([sQuery(id+"F12.wireOp",EDGE,"E38.bottom"),sQuery(id+"F12.wireOp",EDGE,"E38.top"),sQuery(id+"F12.wireOp",EDGE,"E38.left"),sQuery(id+"F12.wireOp",EDGE,"E38.right")])],"isStart":false}),makeQuery(id+"F15.hole-0.opRevolve","SWEPT_FACE",FACE,{"disambiguationData":[OSD([sQuery(id+"F15.hole-0.sketch.wireOp",EDGE,"core_line_2")])]})]});
            var Q26;
            Q26=makeQuery(id+"F14.hole-0.boolean.opBoolean","INTERSECT",EDGE,{"derivedFrom":[makeQuery(id+"F13.opExtrude","CAP_FACE",FACE,{"disambiguationData":[OSD([sQuery(id+"F12.wireOp",EDGE,"E38.bottom"),sQuery(id+"F12.wireOp",EDGE,"E38.top"),sQuery(id+"F12.wireOp",EDGE,"E38.left"),sQuery(id+"F12.wireOp",EDGE,"E38.right")])],"isStart":false}),makeQuery(id+"F14.hole-0.opRevolve","SWEPT_FACE",FACE,{"disambiguationData":[OSD([sQuery(id+"F14.hole-0.sketch.wireOp",EDGE,"core_line_2")])]})]});
            var Q27;
            Q27=makeQuery(id+"F9.hole-0.boolean.opBoolean","COPY",EDGE,{"derivedFrom":makeQuery(id+"F9.hole-0.opRevolve","SWEPT_EDGE",EDGE,{"disambiguationData":[OSD([sQuery(id+"F9.hole-0.sketch.wireOp",EDGE,"core_line_2"),sQuery(id+"F9.hole-0.sketch.wireOp",EDGE,"core_line_3")])]})});
            chamfer(context, id + "F21", {"entities" : qUnion([Q0, Q1, Q2, Q3, Q4, Q5, Q6, Q7, Q8, Q9, Q10, Q11, Q12, Q13, Q14, Q15, Q16, Q17, Q18, Q19, Q20, Q21, Q22, Q23, Q24, Q25, Q26, Q27]), "width" : .2 * mm, "tangentPropagation" : true});
        }
    });
